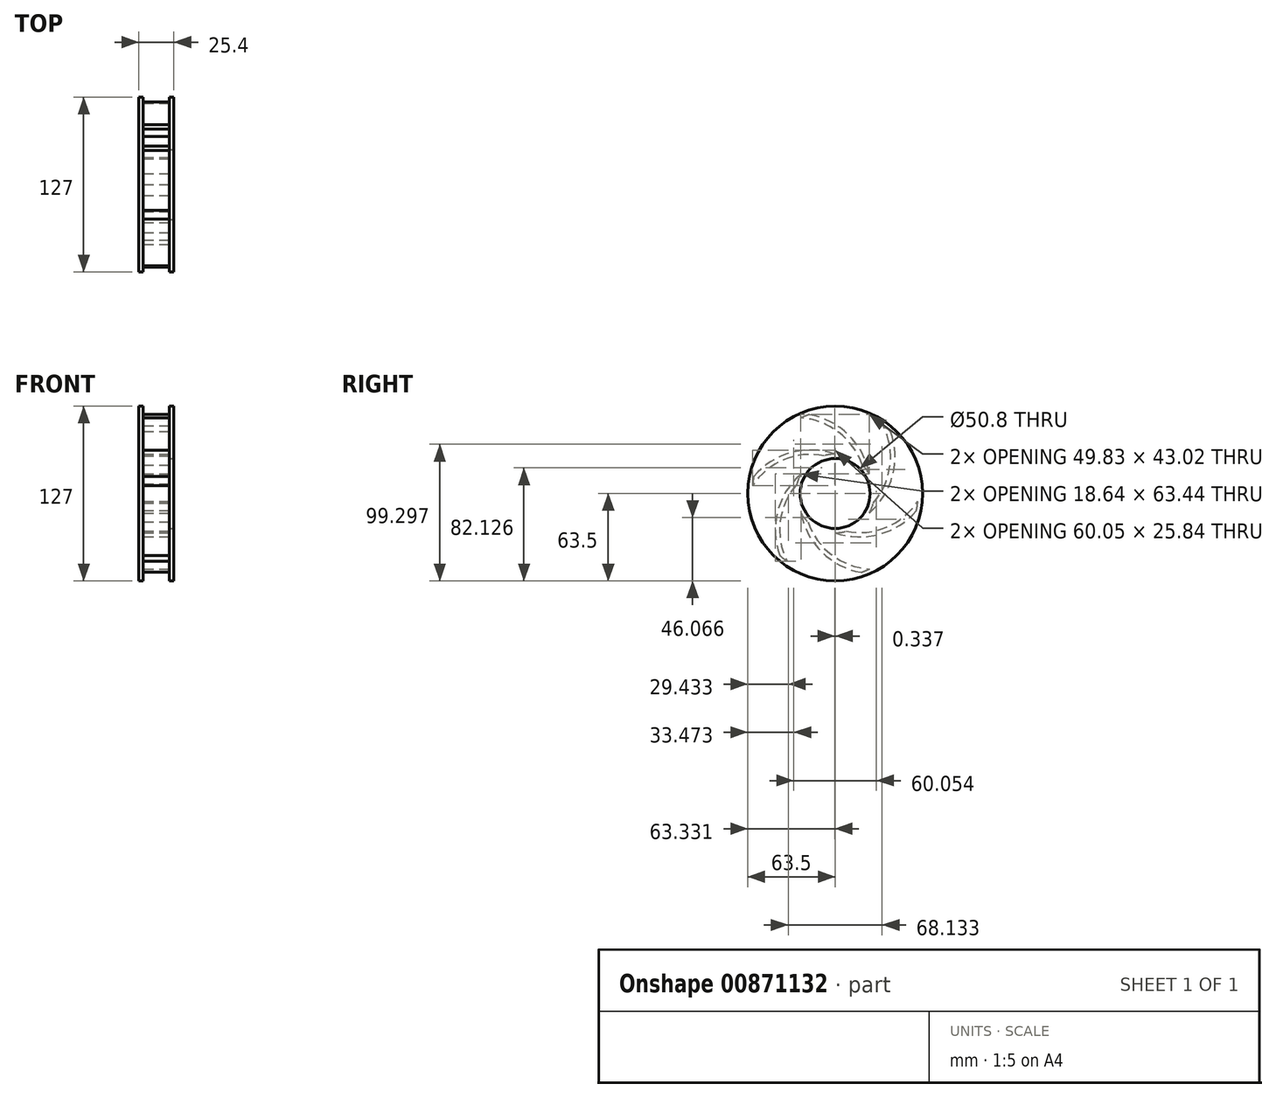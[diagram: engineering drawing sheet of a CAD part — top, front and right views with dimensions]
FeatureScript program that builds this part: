
annotation { "Feature Type Name" : "Feature", "Feature Type Description" : "" }
export const myFeature = defineFeature(function(context is Context, id is Id, definition is map)
    precondition{}
    {
        {
            var Q0;
            Q0=qCreatedBy(makeId("Right.planeOp"),FACE);
            var sketch = newSketch(context, id + "F0", { "sketchPlane" : qUnion([Q0])});
            skCircle(sketch, "E0.0", {"center": v(0, 0) * mm, "radius": 60.33 * mm});
            skCircle(sketch, "E1", {"center": v(0, 0) * mm, "radius": 25.4 * mm});
            skCircle(sketch, "E2", {"center": v(0, 0) * mm, "radius": 28.58 * mm});
            skLineSegment(sketch, "E3", {"start": v(0, 60.33) * mm, "end": v(0, -60.33) * mm, "construction": true});
            skLineSegment(sketch, "E4", {"start": v(-60.33, 0) * mm, "end": v(60.33, 0) * mm, "construction": true});
            skArc(sketch, "E5", {"start": v(0, 28.58) * mm, "mid": v(-32.05, 29.64) * mm, "end": v(-59.05, 12.34) * mm});
            skArc(sketch, "E6.0", {"start": v(-7.95, 27.45) * mm, "mid": v(-37.3, 24.48) * mm, "end": v(-60.05, 5.7) * mm});
            skCircle(sketch, "E7", {"center": v(0, 0) * mm, "radius": 63.5 * mm});
            skSolve(sketch);
        }
        {
            var Q0;
            {var subQ1=sQuery(id+"F0.wireOp",EDGE,"E5");Q0=makeQuery(id+"F0.imprint","IMPRINT",FACE,{"disambiguationData":[TD([[makeQuery(id+"F0.imprint","IMPRINT",EDGE,{"derivedFrom":subQ1}),-1.0]])]});}
            var Q1;
            Q1=makeQuery(id+"F0.imprint","IMPRINT",FACE,{"disambiguationData":[TD([[makeQuery(id+"F0.imprint","IMPRINT",EDGE,{"derivedFrom":sQuery(id+"F0.wireOp",EDGE,"E7")}),1.0]])]});
            var Q2;
            {var subQ1=sQuery(id+"F0.wireOp",EDGE,"E5");Q2=makeQuery(id+"F0.imprint","IMPRINT",FACE,{"disambiguationData":[TD([[makeQuery(id+"F0.imprint","IMPRINT",EDGE,{"derivedFrom":subQ1}),1.0]])]});}
            var Q3;
            Q3=makeQuery(id+"F0.imprint","IMPRINT",FACE,{"disambiguationData":[TD([[makeQuery(id+"F0.imprint","IMPRINT",EDGE,{"derivedFrom":sQuery(id+"F0.wireOp",EDGE,"E1")}),-1.0]])]});
            var Q4;
            {var subQ4=sQuery(id+"F0.wireOp",EDGE,"E6.0");Q4=makeQuery(id+"F0.imprint","IMPRINT",FACE,{"disambiguationData":[TD([[makeQuery(id+"F0.imprint","IMPRINT",EDGE,{"derivedFrom":subQ4}),-1.0]])]});}
            extrude(context, id + "F1", {"entities" : qUnion([Q0, Q1, Q2, Q3, Q4]), "oppositeDirection" : true, "depth" : 3.17 * mm, "offsetDistance" : 25.4 * mm});
        }
        {
            var Q0;
            {var subQ4=sQuery(id+"F0.wireOp",EDGE,"E6.0");Q0=makeQuery(id+"F0.imprint","IMPRINT",FACE,{"disambiguationData":[TD([[makeQuery(id+"F0.imprint","IMPRINT",EDGE,{"derivedFrom":subQ4}),-1.0]])]});}
            extrude(context, id + "F2", {"entities" : qUnion([Q0]), "operationType" : NewBodyOperationType.ADD, "oppositeDirection" : true, "depth" : 22.22 * mm, "offsetDistance" : 25.4 * mm});
        }
        {
            var Q0;
            Q0=makeQuery(id+"F2.opExtrude","SWEPT_FACE",FACE,{"disambiguationData":[OSD([sQuery(id+"F0.wireOp",EDGE,"E5")])]});
            var Q1;
            Q1=makeQuery(id+"F2.opExtrude","CAP_FACE",FACE,{"disambiguationData":[OSD([sQuery(id+"F0.wireOp",EDGE,"E0.0"),sQuery(id+"F0.wireOp",EDGE,"E2"),sQuery(id+"F0.wireOp",EDGE,"E5"),sQuery(id+"F0.wireOp",EDGE,"E6.0")])],"isStart":false});
            var Q2;
            Q2=makeQuery(id+"F2.opExtrude","SWEPT_FACE",FACE,{"disambiguationData":[OSD([sQuery(id+"F0.wireOp",EDGE,"E6.0")])]});
            var Q3;
            Q3=makeQuery(id+"F2.opExtrude","SWEPT_FACE",FACE,{"disambiguationData":[OSD([sQuery(id+"F0.wireOp",EDGE,"E0.0")])]});
            var Q4;
            Q4=makeQuery(id+"F2.opExtrude","SWEPT_FACE",FACE,{"disambiguationData":[OSD([sQuery(id+"F0.wireOp",EDGE,"E2")])]});
            var Q5;
            Q5=makeQuery(id+"F1.opExtrude","CAP_EDGE",EDGE,{"disambiguationData":[OSD([sQuery(id+"F0.wireOp",EDGE,"E1")])],"isStart":true});
            circularPattern(context, id + "F3", {"faces" : qUnion([Q0, Q1, Q2, Q3, Q4]), "axis" : qUnion([Q5]), "angle" : 360 * degree, "instanceCount" : 6, "equalSpace" : true, "patternType" : PatternType.FACE, "computeTransformsWithoutBuiltin" : true});
        }
        {
            var Q0;
            Q0=makeQuery(id+"F3.opPattern","COPY",FACE,{"derivedFrom":makeQuery(id+"F2.opExtrude","CAP_FACE",FACE,{"disambiguationData":[OSD([sQuery(id+"F0.wireOp",EDGE,"E0.0"),sQuery(id+"F0.wireOp",EDGE,"E2"),sQuery(id+"F0.wireOp",EDGE,"E5"),sQuery(id+"F0.wireOp",EDGE,"E6.0")])],"isStart":false}),"instanceName":"4"});
            var sketch = newSketch(context, id + "F4", { "sketchPlane" : qUnion([Q0])});
            skCircle(sketch, "E8", {"center": v(0, 0) * mm, "radius": 63.5 * mm});
            skSolve(sketch);
        }
        {
            var Q0;
            Q0=qSketchRegion(id+"F4",true);
            extrude(context, id + "F5", {"entities" : qUnion([Q0]), "operationType" : NewBodyOperationType.ADD, "depth" : 3.17 * mm, "offsetDistance" : 25.4 * mm});
        }
        {
            var Q0;
            Q0=makeQuery(id+"F1.opExtrude","SWEPT_BODY",BODY,{"disambiguationData":[OSD([sQuery(id+"F0.wireOp",EDGE,"E1"),sQuery(id+"F0.wireOp",EDGE,"E7")])]});
            transform(context, id + "F6", {"entities" : qUnion([Q0]), "transformType" : TransformType.TRANSLATION_3D, "dx" : 12.7 * mm, "dy" : 0 * mm, "dz" : 0 * mm, "makeCopy" : false});
        }
    });
